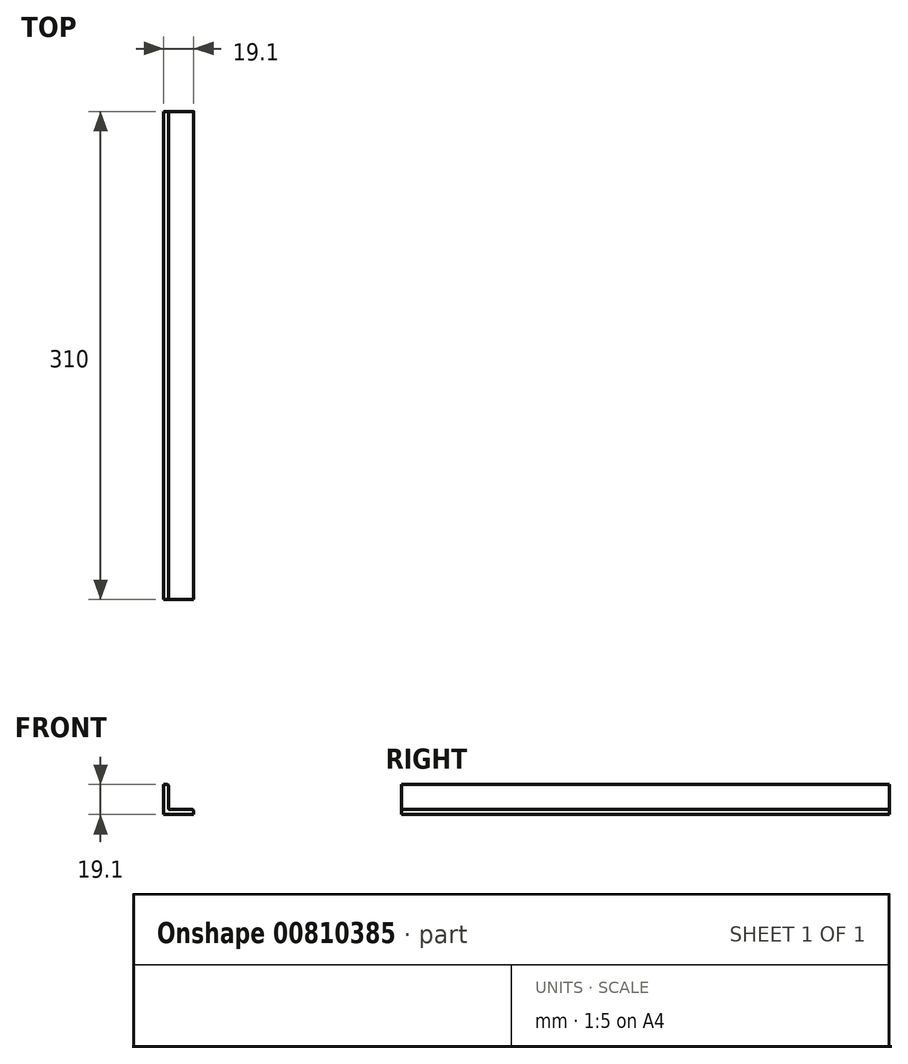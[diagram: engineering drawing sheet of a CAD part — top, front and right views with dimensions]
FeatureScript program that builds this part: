
annotation { "Feature Type Name" : "Feature", "Feature Type Description" : "" }
export const myFeature = defineFeature(function(context is Context, id is Id, definition is map)
    precondition{}
    {
        {
            var Q0;
            Q0=qCreatedBy(makeId("Front.planeOp"),FACE);
            var sketch = newSketch(context, id + "F0", { "sketchPlane" : qUnion([Q0])});
            skLineSegment(sketch, "E0", {"start": v(0, 19.1) * mm, "end": v(0, 0) * mm});
            skLineSegment(sketch, "E1", {"start": v(0, 0) * mm, "end": v(19.1, 0) * mm});
            skLineSegment(sketch, "E2", {"start": v(19.1, 0) * mm, "end": v(19.1, 2.17) * mm});
            skLineSegment(sketch, "E3", {"start": v(18.1, 3.17) * mm, "end": v(4.17, 3.17) * mm});
            skLineSegment(sketch, "E4", {"start": v(3.17, 4.17) * mm, "end": v(3.17, 18.1) * mm});
            skLineSegment(sketch, "E5", {"start": v(2.17, 19.1) * mm, "end": v(0, 19.1) * mm});
            skPoint(sketch, "E6.visualSharp", {"position": v(3.17, 19.1) * mm});
            skArc(sketch, "E6.filletArc", {"start": v(3.17, 18.1) * mm, "mid": v(2.88, 18.8) * mm, "end": v(2.17, 19.1) * mm});
            skPoint(sketch, "E7.visualSharp", {"position": v(19.1, 3.17) * mm});
            skArc(sketch, "E7.filletArc", {"start": v(19.1, 2.17) * mm, "mid": v(18.8, 2.88) * mm, "end": v(18.1, 3.17) * mm});
            skPoint(sketch, "E8.visualSharp", {"position": v(3.17, 3.17) * mm});
            skArc(sketch, "E8.filletArc", {"start": v(3.17, 4.17) * mm, "mid": v(3.46, 3.46) * mm, "end": v(4.17, 3.17) * mm});
            skSolve(sketch);
        }
        {
            var Q0;
            Q0=makeQuery(id+"F0.imprint","IMPRINT",FACE,{"disambiguationData":[TD([[makeQuery(id+"F0.imprint","IMPRINT",EDGE,{"derivedFrom":sQuery(id+"F0.wireOp",EDGE,"E0")}),1.0]])]});
            extrude(context, id + "F1", {"entities" : qUnion([Q0]), "depth" : 310 * mm, "offsetDistance" : 25 * mm});
        }
    });
